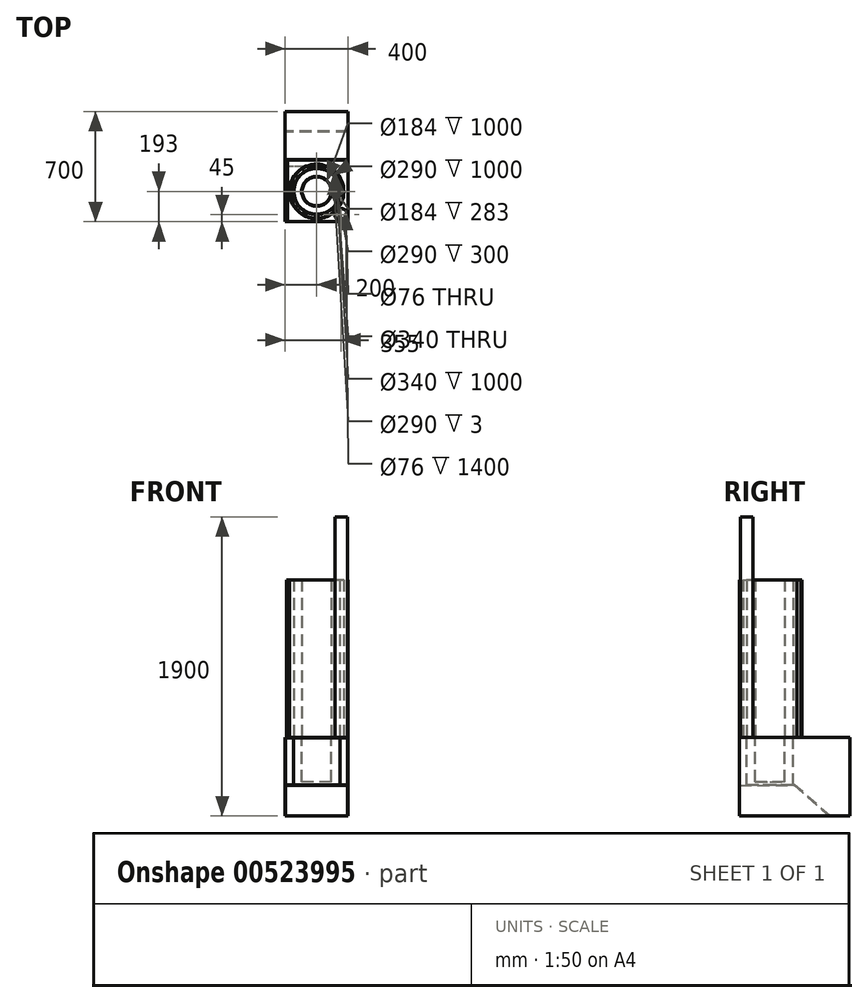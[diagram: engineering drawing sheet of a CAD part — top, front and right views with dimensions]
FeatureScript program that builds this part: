
annotation { "Feature Type Name" : "Feature", "Feature Type Description" : "" }
export const myFeature = defineFeature(function(context is Context, id is Id, definition is map)
    precondition{}
    {
        {
            var Q0;
            Q0=qCreatedBy(makeId("Front.planeOp"),FACE);
            var sketch = newSketch(context, id + "F0", { "sketchPlane" : qUnion([Q0])});
            skLineSegment(sketch, "E0", {"start": v(-197, 0) * mm, "end": v(197, 0) * mm});
            skLineSegment(sketch, "E1", {"start": v(197, 0) * mm, "end": v(197, -497) * mm});
            skLineSegment(sketch, "E2", {"start": v(-197, 0) * mm, "end": v(-197, -497) * mm});
            skLineSegment(sketch, "E3.0", {"start": v(200, 3) * mm, "end": v(200, -497) * mm});
            skLineSegment(sketch, "E3.1", {"start": v(-200, 3) * mm, "end": v(200, 3) * mm});
            skLineSegment(sketch, "E3.2", {"start": v(-200, 3) * mm, "end": v(-200, -497) * mm});
            skLineSegment(sketch, "E4", {"start": v(-200, -497) * mm, "end": v(-197, -497) * mm});
            skLineSegment(sketch, "E5", {"start": v(200, -497) * mm, "end": v(197, -497) * mm});
            skSolve(sketch);
        }
        {
            var Q0;
            Q0=makeQuery(id+"F0.imprint","IMPRINT",FACE,{"disambiguationData":[TD([[makeQuery(id+"F0.imprint","IMPRINT",EDGE,{"derivedFrom":sQuery(id+"F0.wireOp",EDGE,"E0")}),1.0]])]});
            extrude(context, id + "F1", {"entities" : qUnion([Q0]), "oppositeDirection" : true, "depth" : 700 * mm, "offsetDistance" : 25 * mm});
        }
        {
            var Q0;
            Q0=makeQuery(id+"F1.opExtrude","SWEPT_FACE",FACE,{"disambiguationData":[OSD([sQuery(id+"F0.wireOp",EDGE,"E3.1")])]});
            var sketch = newSketch(context, id + "F2", { "sketchPlane" : qUnion([Q0])});
            skLineSegment(sketch, "E6", {"start": v(-200, 193) * mm, "end": v(200, 193) * mm, "construction": true});
            skCircle(sketch, "E7", {"center": v(0, 193) * mm, "radius": 173 * mm});
            skCircle(sketch, "E8.0", {"center": v(0, 193) * mm, "radius": 170 * mm});
            skCircle(sketch, "E9", {"center": v(0, 193) * mm, "radius": 148 * mm});
            skCircle(sketch, "E10.0", {"center": v(0, 193) * mm, "radius": 145 * mm});
            skCircle(sketch, "E11", {"center": v(0, 193) * mm, "radius": 95 * mm});
            skCircle(sketch, "E12.0", {"center": v(0, 193) * mm, "radius": 92 * mm});
            skCircle(sketch, "E13", {"center": v(155, 45) * mm, "radius": 40 * mm});
            skCircle(sketch, "E14.0", {"center": v(155, 45) * mm, "radius": 38 * mm});
            skLineSegment(sketch, "E15", {"start": v(-190, 0) * mm, "end": v(-190, 396) * mm});
            skLineSegment(sketch, "E16", {"start": v(-190, 396) * mm, "end": v(200, 396) * mm});
            skLineSegment(sketch, "E17.0", {"start": v(-185, 391) * mm, "end": v(200, 391) * mm});
            skLineSegment(sketch, "E17.1", {"start": v(-185, 0) * mm, "end": v(-185, 391) * mm});
            skSolve(sketch);
        }
        {
            var Q0;
            Q0=makeQuery(id+"F2.imprint","IMPRINT",FACE,{"disambiguationData":[TD([[makeQuery(id+"F2.imprint","IMPRINT",EDGE,{"derivedFrom":sQuery(id+"F2.wireOp",EDGE,"E14.0")}),1.0]])]});
            var Q1;
            {var subQ0=sQuery(id+"F2.wireOp",EDGE,"5sbHLgVQ-65Wp-SB8w-kyTM-2AFkAULqR3yy");Q1=makeQuery(id+"F2.imprint","IMPRINT",FACE,{"disambiguationData":[TD([[makeQuery(id+"F2.imprint","IMPRINT",EDGE,{"derivedFrom":subQ0}),1.0]])]});}
            var Q2;
            {var subQ0=sQuery(id+"F2.wireOp",EDGE,"4CURtfDP-WfYV-zkIW-vlye-5abwdPXqS3vj");Q2=makeQuery(id+"F2.imprint","IMPRINT",FACE,{"disambiguationData":[TD([[makeQuery(id+"F2.imprint","IMPRINT",EDGE,{"derivedFrom":subQ0}),1.0]])]});}
            extrude(context, id + "F3", {"entities" : qUnion([Q0, Q1, Q2]), "operationType" : NewBodyOperationType.REMOVE, "oppositeDirection" : true, "depth" : 3 * mm, "offsetDistance" : 25 * mm});
        }
        {
            var Q0;
            Q0=makeQuery(id+"F2.imprint","IMPRINT",FACE,{"disambiguationData":[TD([[makeQuery(id+"F2.imprint","IMPRINT",EDGE,{"derivedFrom":sQuery(id+"F2.wireOp",EDGE,"E11")}),1.0]])]});
            extrude(context, id + "F4", {"entities" : qUnion([Q0]), "depth" : 1000 * mm, "offsetDistance" : 25 * mm});
        }
        {
            var Q0;
            Q0=makeQuery(id+"F2.imprint","IMPRINT",FACE,{"disambiguationData":[TD([[makeQuery(id+"F2.imprint","IMPRINT",EDGE,{"derivedFrom":sQuery(id+"F2.wireOp",EDGE,"E10.0")}),-1.0]])]});
            extrude(context, id + "F5", {"entities" : qUnion([Q0]), "depth" : 1000 * mm, "offsetDistance" : 25 * mm});
        }
        {
            var Q0;
            Q0=makeQuery(id+"F2.imprint","IMPRINT",FACE,{"disambiguationData":[TD([[makeQuery(id+"F2.imprint","IMPRINT",EDGE,{"derivedFrom":sQuery(id+"F2.wireOp",EDGE,"E7")}),1.0]])]});
            extrude(context, id + "F6", {"entities" : qUnion([Q0]), "depth" : 1000 * mm, "offsetDistance" : 25 * mm});
        }
        {
            var Q0;
            Q0=makeQuery(id+"F2.imprint","IMPRINT",FACE,{"disambiguationData":[TD([[makeQuery(id+"F2.imprint","IMPRINT",EDGE,{"derivedFrom":sQuery(id+"F2.wireOp",EDGE,"E13")}),1.0]])]});
            extrude(context, id + "F7", {"entities" : qUnion([Q0]), "depth" : 1400 * mm, "offsetDistance" : 25 * mm});
        }
        {
            var Q0;
            {var subQ3=sQuery(id+"F2.wireOp",EDGE,"E15");Q0=makeQuery(id+"F2.imprint","IMPRINT",FACE,{"disambiguationData":[TD([[makeQuery(id+"F2.imprint","IMPRINT",EDGE,{"derivedFrom":subQ3}),-1.0]])]});}
            extrude(context, id + "F8", {"entities" : qUnion([Q0]), "depth" : 1000 * mm, "offsetDistance" : 25 * mm});
        }
        {
            var Q0;
            Q0=makeQuery(id+"F2.imprint","IMPRINT",FACE,{"disambiguationData":[TD([[makeQuery(id+"F2.imprint","IMPRINT",EDGE,{"derivedFrom":sQuery(id+"F2.wireOp",EDGE,"E8.0")}),1.0]])]});
            var Q1;
            Q1=makeQuery(id+"F2.imprint","IMPRINT",FACE,{"disambiguationData":[TD([[makeQuery(id+"F2.imprint","IMPRINT",EDGE,{"derivedFrom":sQuery(id+"F2.wireOp",EDGE,"E12.0")}),1.0]])]});
            var Q2;
            Q2=makeQuery(id+"F2.imprint","IMPRINT",FACE,{"disambiguationData":[TD([[makeQuery(id+"F2.imprint","IMPRINT",EDGE,{"derivedFrom":sQuery(id+"F2.wireOp",EDGE,"E10.0")}),1.0]])]});
            extrude(context, id + "F9", {"entities" : qUnion([Q0, Q1, Q2]), "operationType" : NewBodyOperationType.REMOVE, "oppositeDirection" : true, "depth" : 25 * mm, "offsetDistance" : 25 * mm});
        }
        {
            var Q0;
            Q0=makeQuery(id+"F1.opExtrude","SWEPT_FACE",FACE,{"disambiguationData":[OSD([sQuery(id+"F0.wireOp",EDGE,"E3.2")])]});
            var sketch = newSketch(context, id + "F10", { "sketchPlane" : qUnion([Q0])});
            skLineSegment(sketch, "E18.0.0", {"start": v(0, -497) * mm, "end": v(0, 3) * mm});
            skLineSegment(sketch, "E18.0.1", {"start": v(0, 3) * mm, "end": v(-700, 3) * mm});
            skLineSegment(sketch, "E18.0.2", {"start": v(-700, 3) * mm, "end": v(-700, -497) * mm});
            skLineSegment(sketch, "E18.0.3", {"start": v(-700, -497) * mm, "end": v(0, -497) * mm});
            skLineSegment(sketch, "E19", {"start": v(-574.55, -497) * mm, "end": v(-350, -300) * mm});
            skLineSegment(sketch, "E20", {"start": v(-350, -300) * mm, "end": v(0, -300) * mm});
            skLineSegment(sketch, "E21.0", {"start": v(-348.87, -303) * mm, "end": v(21.36, -303) * mm});
            skLineSegment(sketch, "E21.1", {"start": v(-570, -497) * mm, "end": v(-348.87, -303) * mm});
            skSolve(sketch);
        }
        {
            var Q0;
            {var subQ1=sQuery(id+"F10.wireOp",EDGE,"E19");Q0=makeQuery(id+"F10.imprint","IMPRINT",FACE,{"disambiguationData":[TD([[makeQuery(id+"F10.imprint","IMPRINT",EDGE,{"derivedFrom":subQ1}),-1.0]])]});}
            var Q1;
            Q1=makeQuery(id+"F1.opExtrude","SWEPT_FACE",FACE,{"disambiguationData":[OSD([sQuery(id+"F0.wireOp",EDGE,"E1")])]});
            extrude(context, id + "F11", {"entities" : qUnion([Q0]), "operationType" : NewBodyOperationType.ADD, "endBound" : BoundingType.UP_TO_SURFACE, "oppositeDirection" : true, "depth" : 25 * mm, "endBoundEntityFace" : qUnion([Q1]), "offsetDistance" : 25 * mm});
        }
        {
            var Q0;
            Q0=makeQuery(id+"F2.imprint","IMPRINT",FACE,{"disambiguationData":[TD([[makeQuery(id+"F2.imprint","IMPRINT",EDGE,{"derivedFrom":sQuery(id+"F2.wireOp",EDGE,"E11")}),1.0]])]});
            var Q1;
            Q1=makeQuery(id+"F2.imprint","IMPRINT",FACE,{"disambiguationData":[TD([[makeQuery(id+"F2.imprint","IMPRINT",EDGE,{"derivedFrom":sQuery(id+"F2.wireOp",EDGE,"E12.0")}),1.0]])]});
            extrude(context, id + "F12", {"entities" : qUnion([Q0, Q1]), "operationType" : NewBodyOperationType.REMOVE, "oppositeDirection" : true, "depth" : 299 * mm, "offsetDistance" : 25 * mm});
        }
        {
            var Q0;
            Q0=makeQuery(id+"F2.imprint","IMPRINT",FACE,{"disambiguationData":[TD([[makeQuery(id+"F2.imprint","IMPRINT",EDGE,{"derivedFrom":sQuery(id+"F2.wireOp",EDGE,"E11")}),1.0]])]});
            extrude(context, id + "F13", {"entities" : qUnion([Q0]), "oppositeDirection" : true, "depth" : 283 * mm, "offsetDistance" : 25 * mm});
        }
        {
            var Q0;
            {var subQ2=sQuery(id+"F0.wireOp",EDGE,"E1");Q0=makeQuery(id+"F11.boolean.opBoolean","SPLIT",FACE,{"disambiguationData":[TD([makeQuery(id+"F11.opExtrude","SWEPT_FACE",FACE,{"disambiguationData":[OSD([sQuery(id+"F10.wireOp",EDGE,"E21.0")])]})])],"derivedFrom":makeQuery(id+"F1.opExtrude","SWEPT_FACE",FACE,{"disambiguationData":[OSD([subQ2])]})});}
            var sketch = newSketch(context, id + "F14", { "sketchPlane" : qUnion([Q0])});
            skLineSegment(sketch, "E22.0", {"start": v(0, -318) * mm, "end": v(-365.97, -318) * mm});
            skSolve(sketch);
        }
        {
            var Q0;
            {var subQ0=sQuery(id+"F14.wireOp",EDGE,"E22.0");Q0=makeQuery(id+"F14.imprint","IMPRINT",FACE,{"disambiguationData":[TD([[makeQuery(id+"F14.imprint","IMPRINT",EDGE,{"derivedFrom":subQ0}),1.0]])]});}
            extrude(context, id + "F15", {"entities" : qUnion([Q0]), "operationType" : NewBodyOperationType.REMOVE, "depth" : 338 * mm, "offsetDistance" : 25 * mm});
        }
        {
            var Q0;
            Q0=makeQuery(id+"F9.boolean.opBoolean","SPLIT",FACE,{"disambiguationData":[TD([makeQuery(id+"F9.opExtrude","SWEPT_FACE",FACE,{"disambiguationData":[OSD([sQuery(id+"F2.wireOp",EDGE,"E9")])]})])],"derivedFrom":makeQuery(id+"F1.opExtrude","SWEPT_FACE",FACE,{"disambiguationData":[OSD([sQuery(id+"F0.wireOp",EDGE,"E0")])]})});
            var Q1;
            Q1=makeQuery(id+"F11.opExtrude","SWEPT_FACE",FACE,{"disambiguationData":[OSD([sQuery(id+"F10.wireOp",EDGE,"E20")])]});
            extrude(context, id + "F16", {"entities" : qUnion([Q0]), "endBound" : BoundingType.UP_TO_SURFACE, "depth" : 25 * mm, "endBoundEntityFace" : qUnion([Q1]), "offsetDistance" : 25 * mm});
        }
    });
